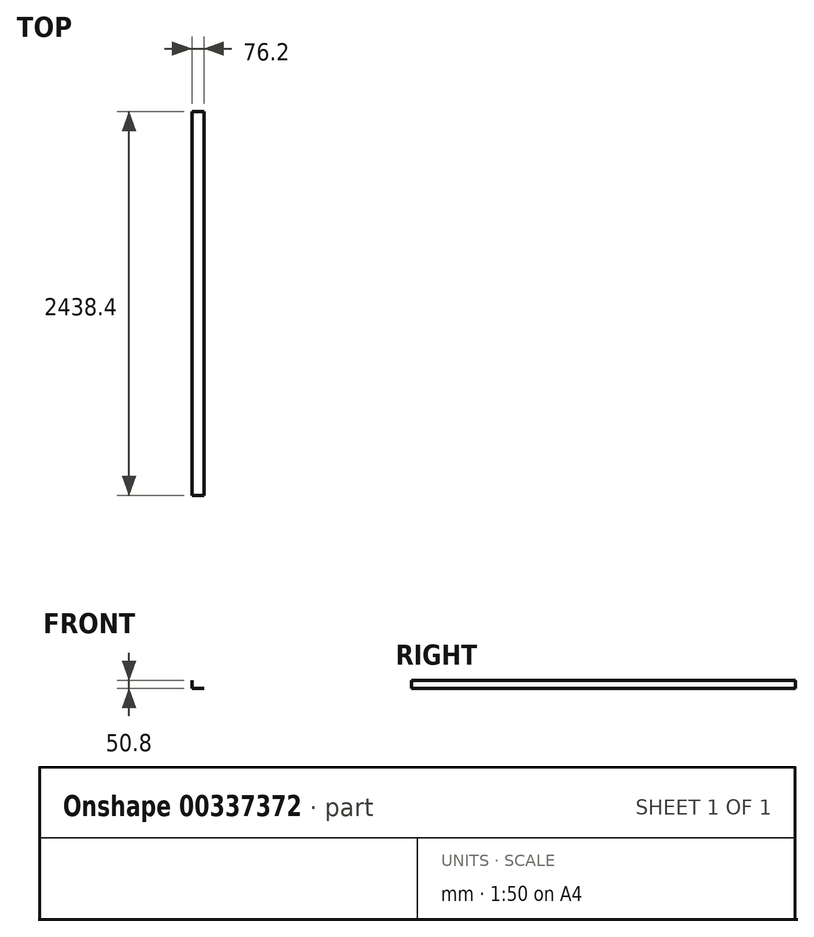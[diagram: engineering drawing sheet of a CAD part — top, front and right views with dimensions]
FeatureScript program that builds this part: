
annotation { "Feature Type Name" : "Feature", "Feature Type Description" : "" }
export const myFeature = defineFeature(function(context is Context, id is Id, definition is map)
    precondition{}
    {
        {
            var Q0;
            Q0=qCreatedBy(makeId("Front.planeOp"),FACE);
            var sketch = newSketch(context, id + "F0", { "sketchPlane" : qUnion([Q0])});
            skLineSegment(sketch, "E0", {"start": v(-99.35, -7.55) * mm, "end": v(-99.35, -58.35) * mm});
            skLineSegment(sketch, "E1", {"start": v(-99.35, -58.35) * mm, "end": v(-23.15, -58.35) * mm});
            skSolve(sketch);
        }
        {
            var Q0;
            Q0 = qSketchRegion(id + "F0", true);
            var Q1;
            Q1=sQuery(id+"F0.wireOp",EDGE,"E0");
            var Q2;
            Q2=sQuery(id+"F0.wireOp",EDGE,"E1");
            extrude(context, id + "F1", {"entities" : qUnion([Q0]), "bodyType" : ToolBodyType.SURFACE, "surfaceEntities" : qUnion([Q1, Q2]), "depth" : 2438.4 * mm});
        }
    });
